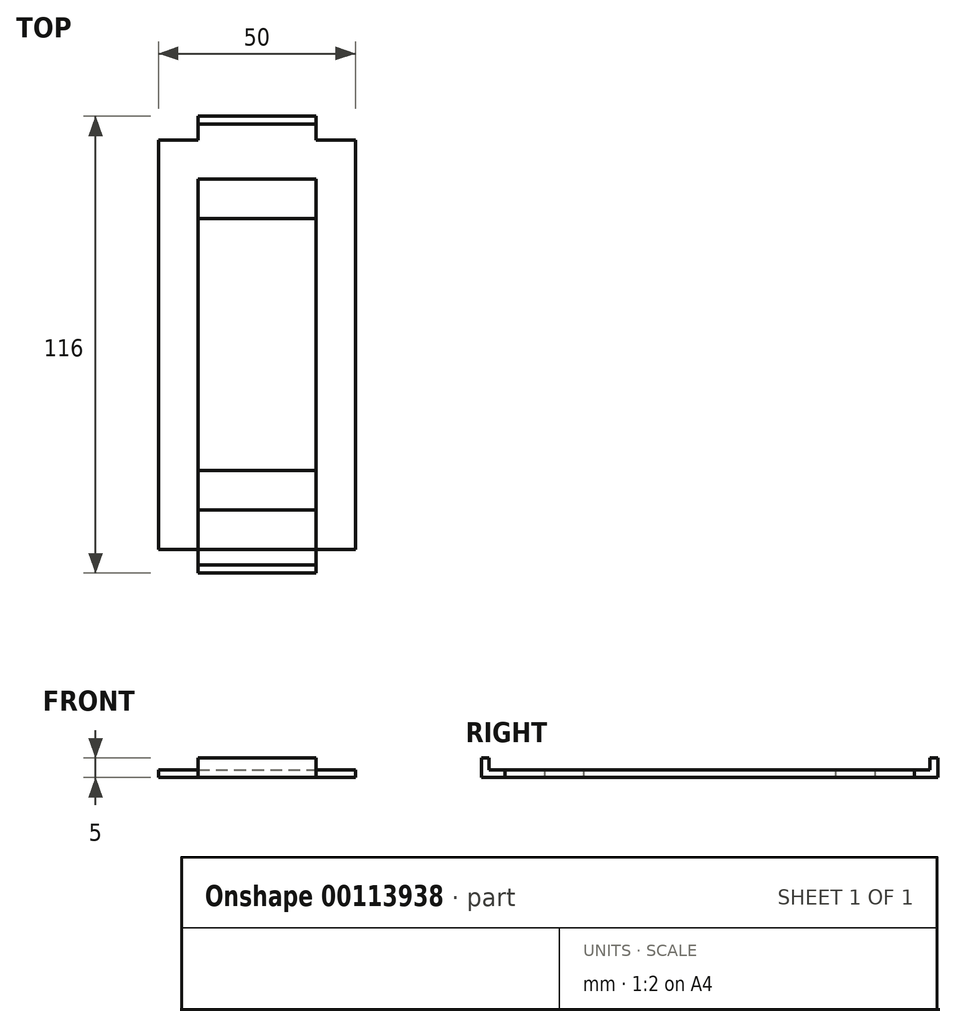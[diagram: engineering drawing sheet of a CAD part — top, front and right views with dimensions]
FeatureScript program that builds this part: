
annotation { "Feature Type Name" : "Feature", "Feature Type Description" : "" }
export const myFeature = defineFeature(function(context is Context, id is Id, definition is map)
    precondition{}
    {
        {
            var Q0;
            Q0=qCreatedBy(makeId("Top.planeOp"),FACE);
            var sketch = newSketch(context, id + "F0", { "sketchPlane" : qUnion([Q0])});
            skLineSegment(sketch, "E0.bottom", {"start": v(15, -58) * mm, "end": v(-15, -58) * mm});
            skLineSegment(sketch, "E0.top", {"start": v(15, 58) * mm, "end": v(-15, 58) * mm});
            skLineSegment(sketch, "E0.left", {"start": v(25, -52) * mm, "end": v(25, 52) * mm});
            skLineSegment(sketch, "E0.right", {"start": v(-25, -52) * mm, "end": v(-25, 52) * mm});
            skPoint(sketch, "E0.middle", {"position": v(0, 0) * mm});
            skLineSegment(sketch, "E1", {"start": v(-15, 58) * mm, "end": v(-15, -58) * mm});
            skLineSegment(sketch, "E2", {"start": v(15, 58) * mm, "end": v(15, -58) * mm});
            skLineSegment(sketch, "E3", {"start": v(-15, 56) * mm, "end": v(15, 56) * mm});
            skLineSegment(sketch, "E4", {"start": v(-15, -56) * mm, "end": v(15, -56) * mm});
            skLineSegment(sketch, "E5", {"start": v(-25, 52) * mm, "end": v(25, 52) * mm});
            skLineSegment(sketch, "E6", {"start": v(-25, -52) * mm, "end": v(25, -52) * mm});
            skPoint(sketch, "E7.orphan", {"position": v(-25, 58) * mm});
            skPoint(sketch, "E8.orphan", {"position": v(25, 58) * mm});
            skPoint(sketch, "E9.orphan", {"position": v(-25, -58) * mm});
            skPoint(sketch, "E10.orphan", {"position": v(25, -58) * mm});
            skLineSegment(sketch, "E11.bottom", {"start": v(-15, 42) * mm, "end": v(15, 42) * mm});
            skLineSegment(sketch, "E11.top", {"start": v(-15, 32) * mm, "end": v(15, 32) * mm});
            skLineSegment(sketch, "E11.left", {"start": v(-15, 42) * mm, "end": v(-15, 32) * mm});
            skLineSegment(sketch, "E11.right", {"start": v(15, 42) * mm, "end": v(15, 32) * mm});
            skLineSegment(sketch, "E12.bottom", {"start": v(-15, -42) * mm, "end": v(15, -42) * mm});
            skLineSegment(sketch, "E12.top", {"start": v(-15, -32) * mm, "end": v(15, -32) * mm});
            skLineSegment(sketch, "E12.left", {"start": v(-15, -42) * mm, "end": v(-15, -32) * mm});
            skLineSegment(sketch, "E12.right", {"start": v(15, -42) * mm, "end": v(15, -32) * mm});
            skSolve(sketch);
        }
        {
            var Q0;
            {var subQ0=sQuery(id+"F0.wireOp",EDGE,"E5");var subQ1=sQuery(id+"F0.wireOp",EDGE,"E1");var subQ2=makeQuery(id+"F0.imprint","INTERSECT",VERTEX,{"derivedFrom":[subQ1,subQ0]});Q0=makeQuery(id+"F0.imprint","IMPRINT",FACE,{"disambiguationData":[TD([[makeQuery(id+"F0.imprint","IMPRINT",EDGE,{"disambiguationData":[TD([[subQ2,-1.0]])],"derivedFrom":subQ1}),1.0]])]});}
            var Q1;
            {var subQ0=sQuery(id+"F0.wireOp",EDGE,"E0.left");Q1=makeQuery(id+"F0.imprint","IMPRINT",FACE,{"disambiguationData":[TD([[makeQuery(id+"F0.imprint","IMPRINT",EDGE,{"derivedFrom":subQ0}),1.0]])]});}
            var Q2;
            {var subQ0=sQuery(id+"F0.wireOp",EDGE,"E3");Q2=makeQuery(id+"F0.imprint","IMPRINT",FACE,{"disambiguationData":[TD([[makeQuery(id+"F0.imprint","IMPRINT",EDGE,{"derivedFrom":subQ0}),-1.0]])]});}
            var Q3;
            {var subQ0=sQuery(id+"F0.wireOp",EDGE,"E4");Q3=makeQuery(id+"F0.imprint","IMPRINT",FACE,{"disambiguationData":[TD([[makeQuery(id+"F0.imprint","IMPRINT",EDGE,{"derivedFrom":subQ0}),1.0]])]});}
            var Q4;
            {var subQ0=sQuery(id+"F0.wireOp",EDGE,"E0.bottom");Q4=makeQuery(id+"F0.imprint","IMPRINT",FACE,{"disambiguationData":[TD([[makeQuery(id+"F0.imprint","IMPRINT",EDGE,{"derivedFrom":subQ0}),-1.0]])]});}
            var Q5;
            {var subQ0=sQuery(id+"F0.wireOp",EDGE,"E0.top");Q5=makeQuery(id+"F0.imprint","IMPRINT",FACE,{"disambiguationData":[TD([[makeQuery(id+"F0.imprint","IMPRINT",EDGE,{"derivedFrom":subQ0}),1.0]])]});}
            var Q6;
            {var subQ0=sQuery(id+"F0.wireOp",EDGE,"E0.right");Q6=makeQuery(id+"F0.imprint","IMPRINT",FACE,{"disambiguationData":[TD([[makeQuery(id+"F0.imprint","IMPRINT",EDGE,{"derivedFrom":subQ0}),-1.0]])]});}
            var Q7;
            {var subQ0=sQuery(id+"F0.wireOp",EDGE,"E4");Q7=makeQuery(id+"F0.imprint","IMPRINT",FACE,{"disambiguationData":[TD([[makeQuery(id+"F0.imprint","IMPRINT",EDGE,{"derivedFrom":subQ0}),1.0]])]});}
            extrude(context, id + "F1", {"entities" : qUnion([Q0, Q1, Q2, Q3, Q4, Q5, Q6, Q7]), "depth" : 2 * mm});
        }
        {
            var Q0;
            {var subQ2=sQuery(id+"F0.wireOp",EDGE,"E4");Q0=makeQuery(id+"F0.imprint","IMPRINT",FACE,{"disambiguationData":[TD([[makeQuery(id+"F0.imprint","IMPRINT",EDGE,{"derivedFrom":subQ2}),-1.0]])]});}
            var Q1;
            {var subQ0=sQuery(id+"F0.wireOp",EDGE,"E0.top");Q1=makeQuery(id+"F0.imprint","IMPRINT",FACE,{"disambiguationData":[TD([[makeQuery(id+"F0.imprint","IMPRINT",EDGE,{"derivedFrom":subQ0}),1.0]])]});}
            extrude(context, id + "F2", {"entities" : qUnion([Q0, Q1]), "operationType" : NewBodyOperationType.ADD, "depth" : 5 * mm});
        }
        {
            var Q0;
            {var subQ0=sQuery(id+"F0.wireOp",EDGE,"E11.top");Q0=makeQuery(id+"F0.imprint","IMPRINT",FACE,{"disambiguationData":[TD([[makeQuery(id+"F0.imprint","IMPRINT",EDGE,{"derivedFrom":subQ0}),-1.0]])]});}
            var Q1;
            {var subQ0=sQuery(id+"F0.wireOp",EDGE,"E12.bottom");Q1=makeQuery(id+"F0.imprint","IMPRINT",FACE,{"disambiguationData":[TD([[makeQuery(id+"F0.imprint","IMPRINT",EDGE,{"derivedFrom":subQ0}),-1.0]])]});}
            extrude(context, id + "F3", {"entities" : qUnion([Q0, Q1]), "depth" : 2 * mm});
        }
    });
